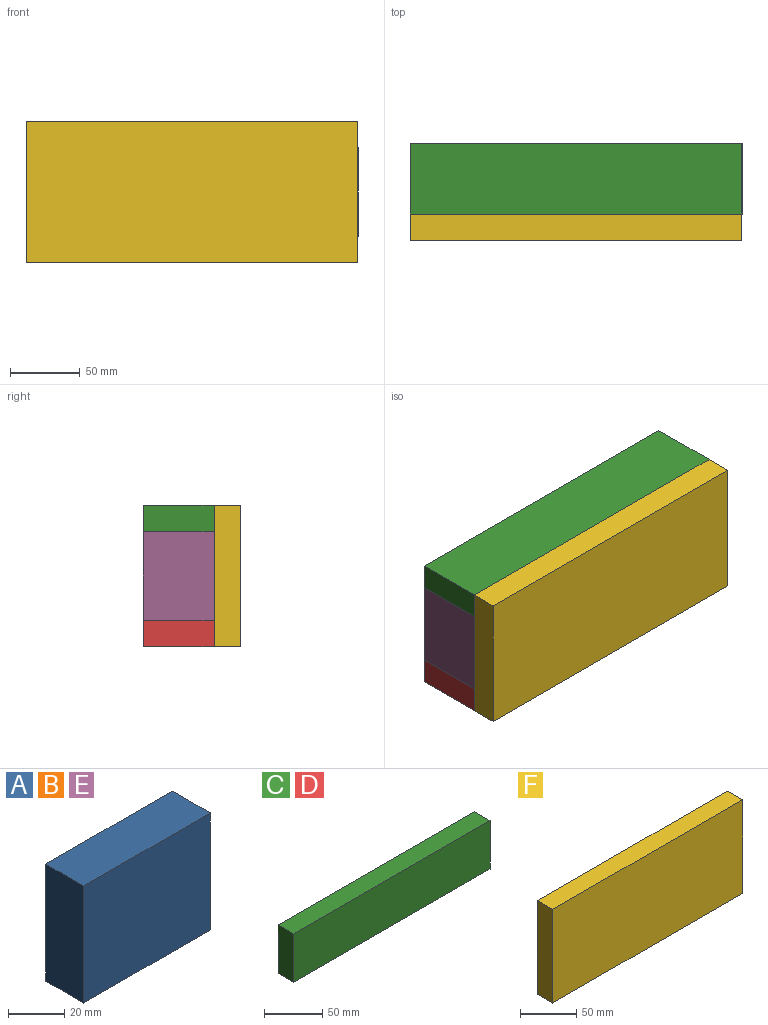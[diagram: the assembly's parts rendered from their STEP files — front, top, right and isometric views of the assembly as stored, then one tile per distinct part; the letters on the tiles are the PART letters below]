
ASSEMBLY  parts=6 mates=6
PART A: 6 faces, bbox 63.5x19.1x50.8 mm
  f0: plane 50.8x19.05mm, normal (-1,0,0), area 967.7mm2, adj f1,f3,f4,f5
  f1: plane 63.5x50.8mm, normal (0,-1,0), area 3225.8mm2, adj f0,f2,f4,f5
  f2: plane 50.8x19.05mm, normal (1,0,0), area 967.7mm2, adj f1,f3,f4,f5
  f3: plane 63.5x50.8mm, normal (0,1,0), area 3225.8mm2, adj f0,f2,f4,f5
  f4: plane 63.5x19.05mm, normal (0,0,1), area 1209.7mm2, adj f0,f1,f2,f3
  f5: plane 63.5x19.05mm, normal (0,0,-1), area 1209.7mm2, adj f0,f1,f2,f3
PART B: same geometry as A
PART C: 6 faces, bbox 238.1x19.1x50.8 mm
  f0: plane 50.8x19.05mm, normal (-1,0,0), area 967.7mm2, adj f1,f3,f4,f5
  f1: plane 238.13x50.8mm, normal (0,-1,0), area 12096.8mm2, adj f0,f2,f4,f5
  f2: plane 50.8x19.05mm, normal (1,0,0), area 967.7mm2, adj f1,f3,f4,f5
  f3: plane 238.13x50.8mm, normal (0,1,0), area 12096.8mm2, adj f0,f2,f4,f5
  f4: plane 238.13x19.05mm, normal (0,0,1), area 4536.3mm2, adj f0,f1,f2,f3
  f5: plane 238.13x19.05mm, normal (0,0,-1), area 4536.3mm2, adj f0,f1,f2,f3
PART D: same geometry as C
PART E: same geometry as A
PART F: 6 faces, bbox 238.1x19.1x101.6 mm
  f0: plane 101.6x19.05mm, normal (-1,0,0), area 1935.5mm2, adj f1,f3,f4,f5
  f1: plane 238.13x101.6mm, normal (0,-1,0), area 24193.5mm2, adj f0,f2,f4,f5
  f2: plane 101.6x19.05mm, normal (1,0,0), area 1935.5mm2, adj f1,f3,f4,f5
  f3: plane 238.13x101.6mm, normal (0,1,0), area 24193.5mm2, adj f0,f2,f4,f5
  f4: plane 238.13x19.05mm, normal (0,0,1), area 4536.3mm2, adj f0,f1,f2,f3
  f5: plane 238.13x19.05mm, normal (0,0,-1), area 4536.3mm2, adj f0,f1,f2,f3
PLACE A rot(axis=(0.58,0.58,-0.58),120deg) t=(89.41,147.35,7.81)mm
PLACE B rot(axis=(-0.58,-0.58,-0.58),120deg) t=(198.95,96.55,-55.69)mm
PLACE C rot(axis=(1,0,0),90deg) t=(-20.13,147.35,7.81)mm
PLACE D rot(axis=(-1,0,0),90deg) t=(-20.13,96.55,-55.69)mm
PLACE E rot(axis=(-0.58,-0.58,-0.58),120deg) t=(-20.13,96.55,-55.69)mm
PLACE F t=(-20.13,77.5,-74.74)mm
MATE fastened C.f4 <-> F.f3  axis (0,-1,0) through (-20.13,96.55,26.86)mm
MATE fastened E.f0 <-> D.f1  axis (0,0,-1) through (-20.13,147.35,-55.69)mm
MATE fastened B.f2 <-> C.f1  axis (0,0,1) through (218,147.35,7.81)mm
MATE planar A.f0 <-> C.f1  axis (0,0,1) through (98.94,121.95,7.81)mm
MATE fastened D.f5 <-> F.f3  axis (0,-1,0) through (-20.13,96.55,-74.74)mm
MATE fastened F.f3 <-> A.f4  axis (0,1,0) through (98.94,96.55,-23.94)mm
